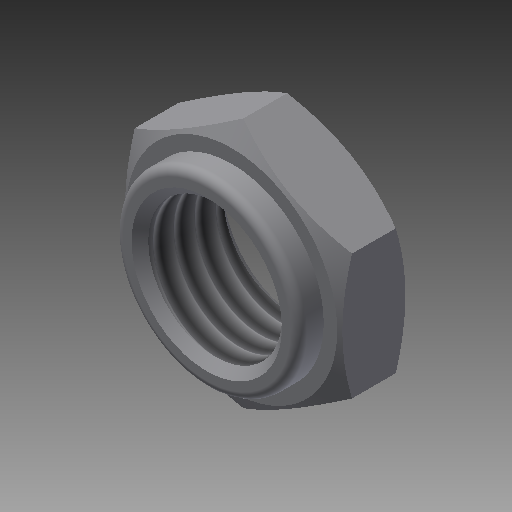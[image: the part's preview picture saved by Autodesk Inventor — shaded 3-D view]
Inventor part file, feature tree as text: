
AUTODESK INVENTOR PART (.ipt)
format: ipt  version: 2019 (Build 230136000, 136)  size: 183,808 bytes
history: native  units: mm
features: extrude x2, sketch x2, other x2, hole x1, thread x1, chamfer x1, revolve x1, fillet x1
ambient origin geometry x8: Origin, YZ Plane, XZ Plane, XY Plane, X Axis, Y Axis, Z Axis, Center Point
bodies: Solido1 (feature_tree)
feature tree (11):
  extrude  "Estrusione1"  Depth=13.0mm
  extrude  "Estrusione2"  Depth=4.0mm TaperAngle=0.0deg
  sketch  "Schizzo3"
  other  "Piano di lavoro1"
  hole  "Foro1"  [1 undecoded]
  thread  "Filettatura1"
  chamfer  "Smusso1"  Distance=11.0mm
  revolve  "Rivoluzione2"
  fillet  "Raccordo1"  [1 undecoded]
  sketch  "Schizzo1"
  other  "Linea chiusa proiettata1"
note: 2 required parameter values undecoded (feature->parameter linkage not recoverable at this tier; creation-order binding heuristic only, values carry confidence <= 0.55)
